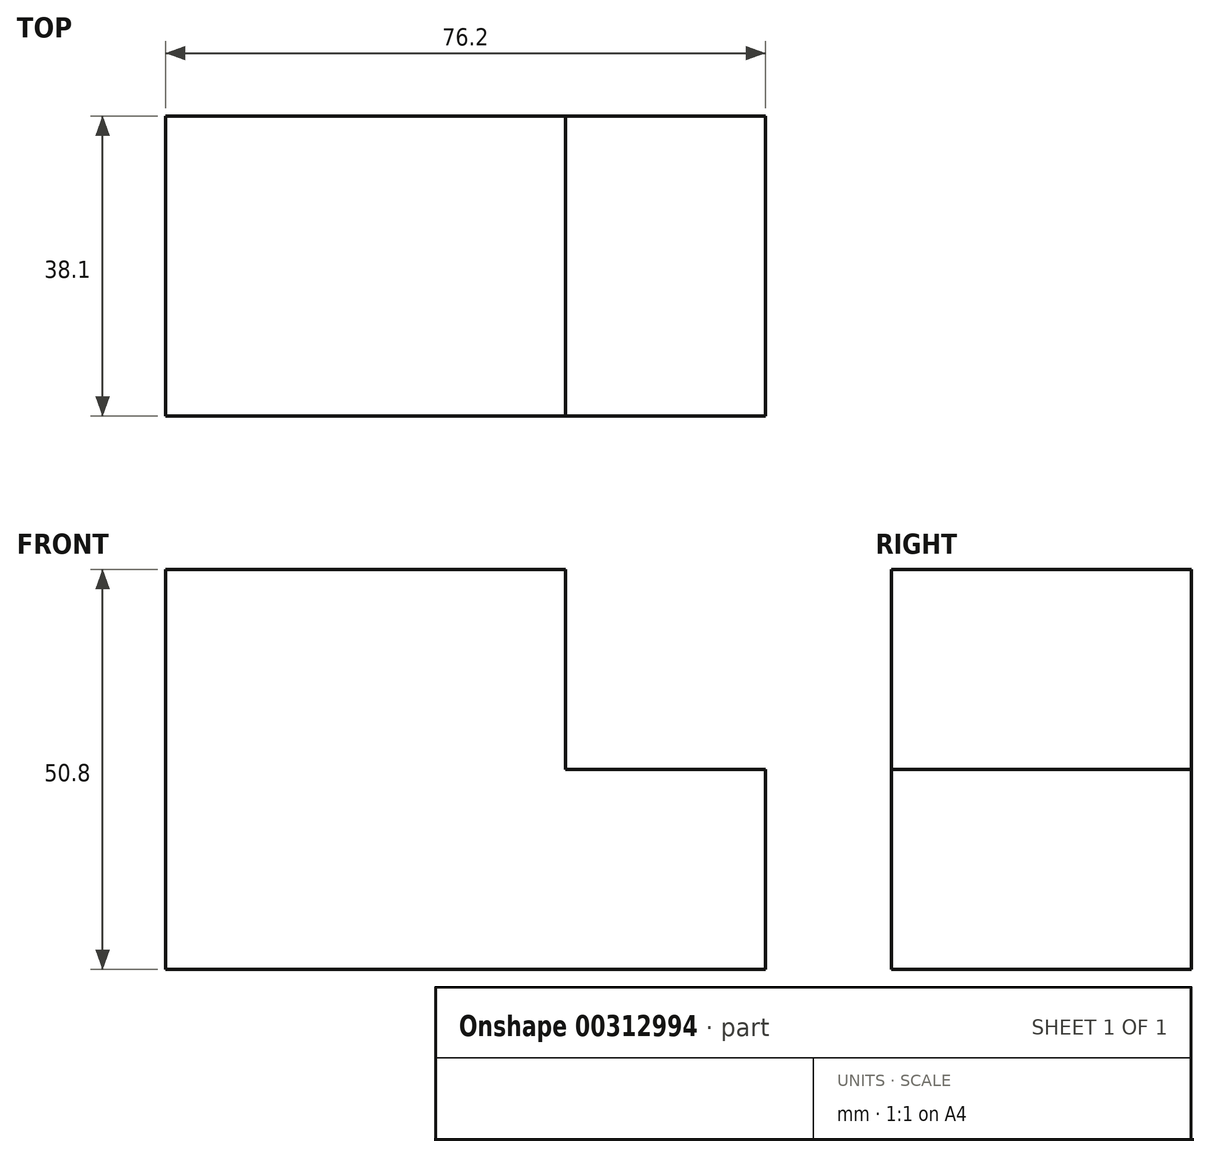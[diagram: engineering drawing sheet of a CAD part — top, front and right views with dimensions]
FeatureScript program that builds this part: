
annotation { "Feature Type Name" : "Feature", "Feature Type Description" : "" }
export const myFeature = defineFeature(function(context is Context, id is Id, definition is map)
    precondition{}
    {
        {
            var Q0;
            Q0=qCreatedBy(makeId("Front.planeOp"),FACE);
            var sketch = newSketch(context, id + "F0", { "sketchPlane" : qUnion([Q0])});
            skLineSegment(sketch, "E0", {"start": v(-41.24, -36.68) * mm, "end": v(34.96, -36.68) * mm});
            skLineSegment(sketch, "E1", {"start": v(34.96, -36.68) * mm, "end": v(34.96, -11.28) * mm});
            skLineSegment(sketch, "E2", {"start": v(34.96, -11.28) * mm, "end": v(9.56, -11.28) * mm});
            skLineSegment(sketch, "E3", {"start": v(9.56, -11.28) * mm, "end": v(9.56, 14.12) * mm});
            skLineSegment(sketch, "E4", {"start": v(9.56, 14.12) * mm, "end": v(-41.24, 14.12) * mm});
            skLineSegment(sketch, "E5", {"start": v(-41.24, 14.12) * mm, "end": v(-41.24, -36.68) * mm});
            skSolve(sketch);
        }
        {
            var Q0;
            Q0=makeQuery(id+"F0.imprint","IMPRINT",FACE,{"disambiguationData":[TD([[makeQuery(id+"F0.imprint","IMPRINT",EDGE,{"derivedFrom":sQuery(id+"F0.wireOp",EDGE,"E0")}),1.0]])]});
            extrude(context, id + "F1", {"entities" : qUnion([Q0]), "oppositeDirection" : true, "depth" : 38.1 * mm});
        }
    });
